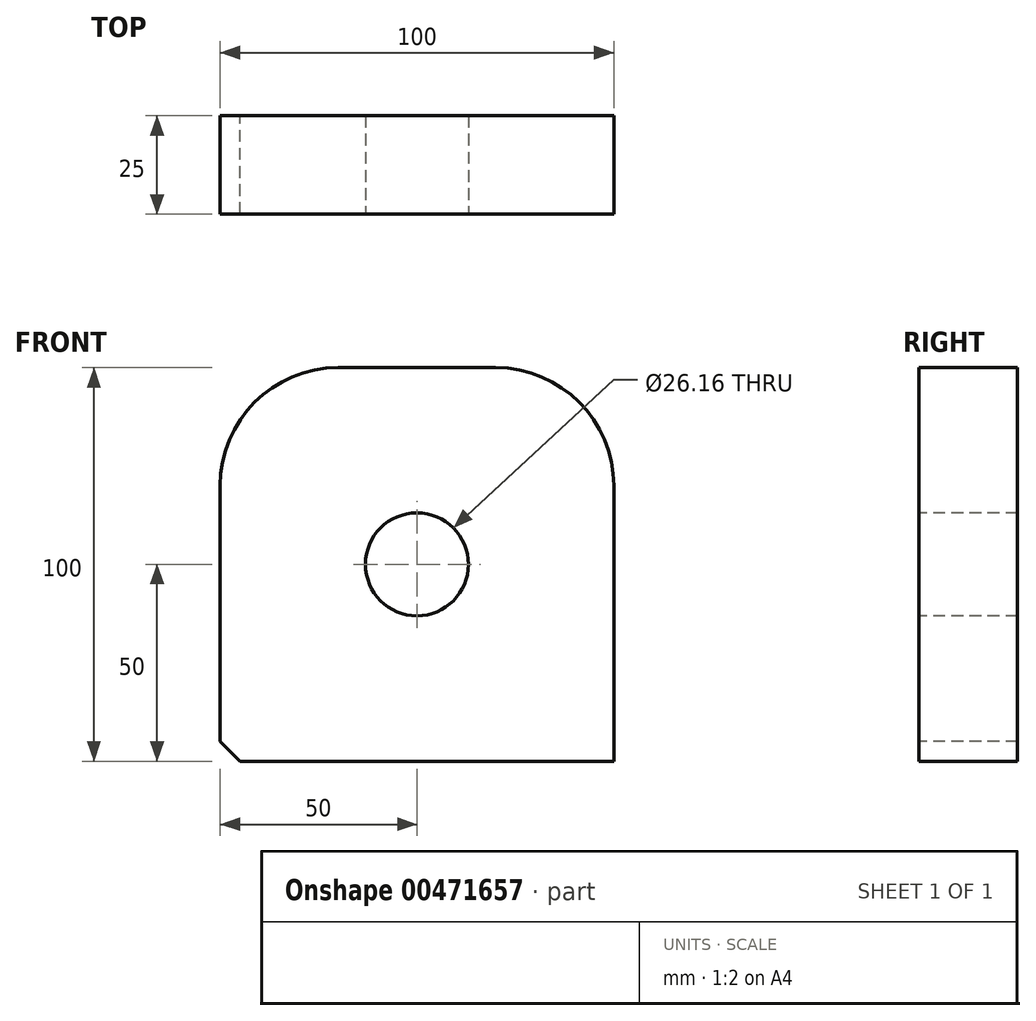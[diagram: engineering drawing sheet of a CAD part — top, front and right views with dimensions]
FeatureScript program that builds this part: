
annotation { "Feature Type Name" : "Feature", "Feature Type Description" : "" }
export const myFeature = defineFeature(function(context is Context, id is Id, definition is map)
    precondition{}
    {
        {
            var Q0;
            Q0=qCreatedBy(makeId("Front.planeOp"),FACE);
            var sketch = newSketch(context, id + "F0", { "sketchPlane" : qUnion([Q0])});
            skLineSegment(sketch, "E0.bottom", {"start": v(50, 50) * mm, "end": v(-50, 50) * mm});
            skLineSegment(sketch, "E0.top", {"start": v(50, -50) * mm, "end": v(-50, -50) * mm});
            skLineSegment(sketch, "E0.left", {"start": v(50, 50) * mm, "end": v(50, -50) * mm});
            skLineSegment(sketch, "E0.right", {"start": v(-50, 50) * mm, "end": v(-50, -50) * mm});
            skPoint(sketch, "E0.middle", {"position": v(0, 0) * mm});
            skSolve(sketch);
        }
        {
            var Q0;
            Q0 = qSketchRegion(id + "F0", true);
            extrude(context, id + "F1", {"entities" : qUnion([Q0]), "depth" : 25 * mm});
        }
        {
            var Q0;
            Q0=makeQuery(id+"F1.opExtrude","SWEPT_EDGE",EDGE,{"disambiguationData":[OSD([sQuery(id+"F0.wireOp",EDGE,"E0.bottom"),sQuery(id+"F0.wireOp",EDGE,"E0.right")])]});
            var Q1;
            Q1=makeQuery(id+"F1.opExtrude","SWEPT_EDGE",EDGE,{"disambiguationData":[OSD([sQuery(id+"F0.wireOp",EDGE,"E0.bottom"),sQuery(id+"F0.wireOp",EDGE,"E0.left")])]});
            fillet(context, id + "F2", {"entities" : qUnion([Q0, Q1]), "radius" : 30 * mm, "tangentPropagation" : true, "allowEdgeOverflow" : false});
        }
        {
            var Q0;
            Q0=makeQuery(id+"F1.opExtrude","SWEPT_EDGE",EDGE,{"disambiguationData":[OSD([sQuery(id+"F0.wireOp",EDGE,"E0.top"),sQuery(id+"F0.wireOp",EDGE,"E0.right")])]});
            chamfer(context, id + "F3", {"entities" : qUnion([Q0]), "width" : 5 * mm, "tangentPropagation" : true});
        }
        {
            var Q0;
            Q0=makeQuery(id+"F1.opExtrude","CAP_FACE",FACE,{"disambiguationData":[OSD([sQuery(id+"F0.wireOp",EDGE,"E0.bottom"),sQuery(id+"F0.wireOp",EDGE,"E0.top"),sQuery(id+"F0.wireOp",EDGE,"E0.left"),sQuery(id+"F0.wireOp",EDGE,"E0.right")])],"isStart":false});
            var sketch = newSketch(context, id + "F4", { "sketchPlane" : qUnion([Q0])});
            skCircle(sketch, "E1", {"center": v(0, 0) * mm, "radius": 13.08 * mm});
            skSolve(sketch);
        }
        {
            var Q0;
            Q0 = qSketchRegion(id + "F4", true);
            extrude(context, id + "F5", {"entities" : qUnion([Q0]), "operationType" : NewBodyOperationType.REMOVE, "oppositeDirection" : true, "depth" : 25 * mm});
        }
    });
